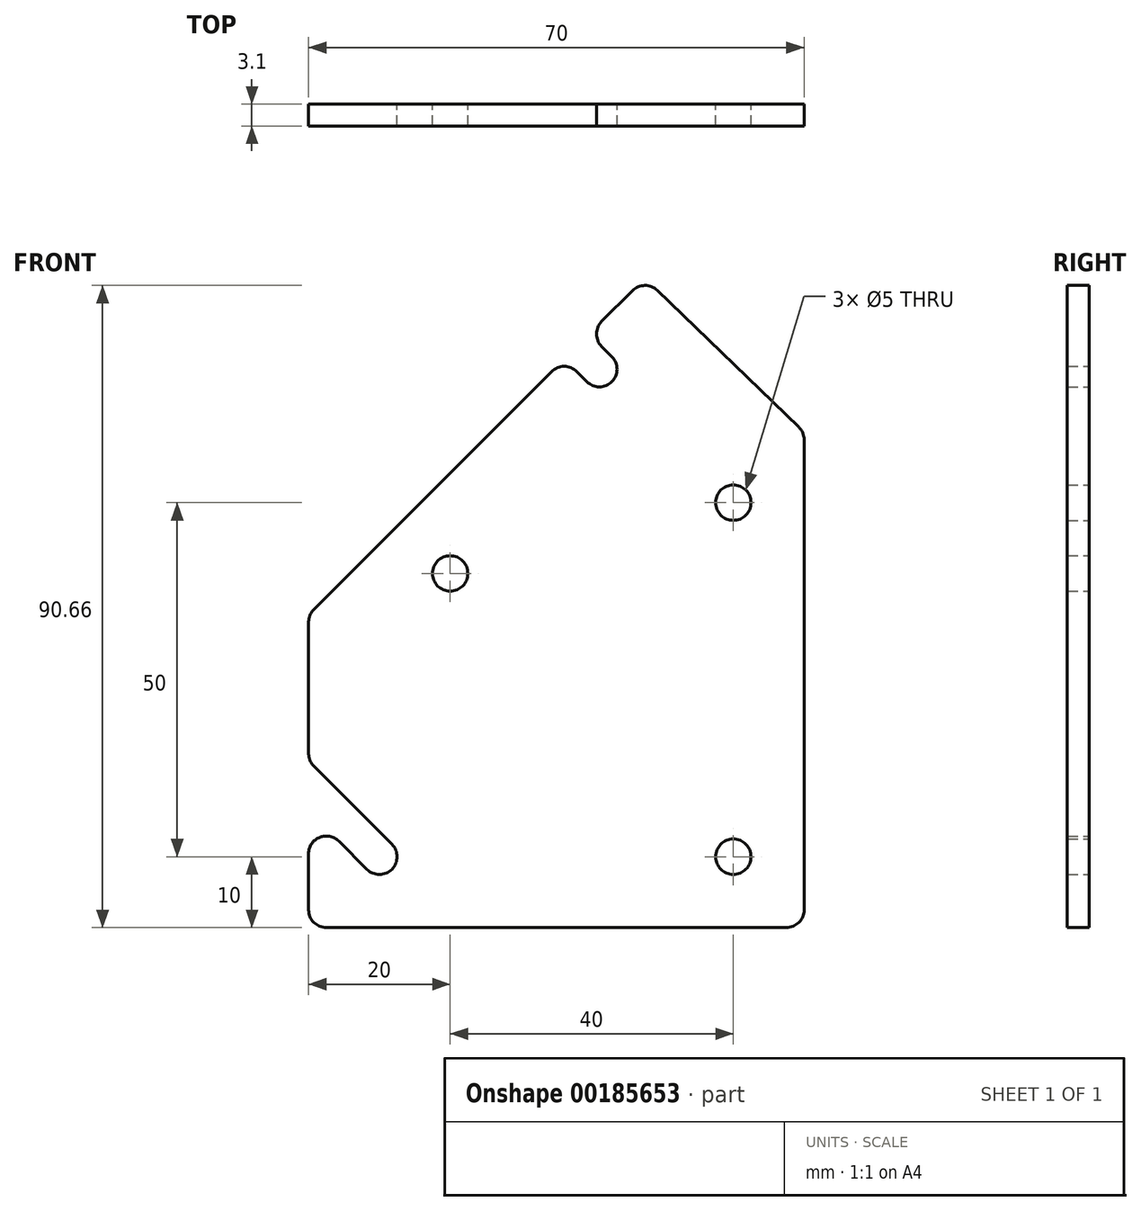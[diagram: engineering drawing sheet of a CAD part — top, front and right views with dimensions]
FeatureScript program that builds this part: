
annotation { "Feature Type Name" : "Feature", "Feature Type Description" : "" }
export const myFeature = defineFeature(function(context is Context, id is Id, definition is map)
    precondition{}
    {
        {
            var Q0;
            Q0=qCreatedBy(makeId("Front.planeOp"),FACE);
            var sketch = newSketch(context, id + "F0", { "sketchPlane" : qUnion([Q0])});
            skLineSegment(sketch, "E0", {"start": v(0, 0) * mm, "end": v(0, 69.94) * mm});
            skLineSegment(sketch, "E1", {"start": v(0, 69.94) * mm, "end": v(-22.5, 91.67) * mm});
            skLineSegment(sketch, "E2", {"start": v(-22.5, 91.67) * mm, "end": v(-30.36, 83.81) * mm});
            skLineSegment(sketch, "E3", {"start": v(-70, 44.17) * mm, "end": v(-70, 23.54) * mm});
            skLineSegment(sketch, "E4", {"start": v(-70, 0) * mm, "end": v(0, 0) * mm});
            skCircle(sketch, "E5", {"center": v(-10, 10) * mm, "radius": 2.5 * mm});
            skCircle(sketch, "E6", {"center": v(-10, 60) * mm, "radius": 2.5 * mm});
            skArc(sketch, "E7", {"start": v(-61.77, 8.23) * mm, "mid": v(-58.23, 8.23) * mm, "end": v(-58.23, 11.77) * mm});
            skCircle(sketch, "E8", {"center": v(-50, 50) * mm, "radius": 2.5 * mm});
            skArc(sketch, "E9", {"start": v(-30.69, 77.07) * mm, "mid": v(-27.15, 77.07) * mm, "end": v(-27.15, 80.6) * mm});
            skLineSegment(sketch, "E10", {"start": v(-27.15, 80.6) * mm, "end": v(-30.36, 83.81) * mm});
            skLineSegment(sketch, "E11", {"start": v(-30.69, 77.07) * mm, "end": v(-33.9, 80.28) * mm});
            skLineSegment(sketch, "E12.trimOffspring", {"start": v(-33.9, 80.28) * mm, "end": v(-70, 44.17) * mm});
            skLineSegment(sketch, "E13", {"start": v(-58.23, 11.77) * mm, "end": v(-70, 23.54) * mm});
            skLineSegment(sketch, "E14", {"start": v(-61.77, 8.23) * mm, "end": v(-70, 16.46) * mm});
            skLineSegment(sketch, "E15.trimOffspring", {"start": v(-70, 16.46) * mm, "end": v(-70, 0) * mm});
            skSolve(sketch);
        }
        {
            var Q0;
            Q0=makeQuery(id+"F0.imprint","IMPRINT",FACE,{"disambiguationData":[TD([[makeQuery(id+"F0.imprint","IMPRINT",EDGE,{"derivedFrom":sQuery(id+"F0.wireOp",EDGE,"E0")}),1.0]])]});
            extrude(context, id + "F1", {"entities" : qUnion([Q0]), "depth" : 3.1 * mm});
        }
        {
            var Q0;
            Q0=makeQuery(id+"F1.opExtrude","SWEPT_EDGE",EDGE,{"disambiguationData":[OSD([sQuery(id+"F0.wireOp",EDGE,"E2"),sQuery(id+"F0.wireOp",EDGE,"E10")])]});
            var Q1;
            Q1=makeQuery(id+"F1.opExtrude","SWEPT_EDGE",EDGE,{"disambiguationData":[OSD([sQuery(id+"F0.wireOp",EDGE,"E11"),sQuery(id+"F0.wireOp",EDGE,"E12.trimOffspring")])]});
            var Q2;
            Q2=makeQuery(id+"F1.opExtrude","SWEPT_EDGE",EDGE,{"disambiguationData":[OSD([sQuery(id+"F0.wireOp",EDGE,"E3"),sQuery(id+"F0.wireOp",EDGE,"E13")])]});
            var Q3;
            Q3=makeQuery(id+"F1.opExtrude","SWEPT_EDGE",EDGE,{"disambiguationData":[OSD([sQuery(id+"F0.wireOp",EDGE,"E14"),sQuery(id+"F0.wireOp",EDGE,"E15.trimOffspring")])]});
            var Q4;
            Q4=makeQuery(id+"F1.opExtrude","SWEPT_EDGE",EDGE,{"disambiguationData":[OSD([sQuery(id+"F0.wireOp",EDGE,"E4"),sQuery(id+"F0.wireOp",EDGE,"E15.trimOffspring")])]});
            var Q5;
            Q5=makeQuery(id+"F1.opExtrude","SWEPT_EDGE",EDGE,{"disambiguationData":[OSD([sQuery(id+"F0.wireOp",EDGE,"E1"),sQuery(id+"F0.wireOp",EDGE,"E2")])]});
            var Q6;
            Q6=makeQuery(id+"F1.opExtrude","SWEPT_EDGE",EDGE,{"disambiguationData":[OSD([sQuery(id+"F0.wireOp",EDGE,"E0"),sQuery(id+"F0.wireOp",EDGE,"E4")])]});
            var Q7;
            Q7=makeQuery(id+"F1.opExtrude","SWEPT_EDGE",EDGE,{"disambiguationData":[OSD([sQuery(id+"F0.wireOp",EDGE,"E0"),sQuery(id+"F0.wireOp",EDGE,"E1")])]});
            var Q8;
            Q8=makeQuery(id+"F1.opExtrude","SWEPT_EDGE",EDGE,{"disambiguationData":[OSD([sQuery(id+"F0.wireOp",EDGE,"E3"),sQuery(id+"F0.wireOp",EDGE,"E12.trimOffspring")])]});
            fillet(context, id + "F2", {"entities" : qUnion([Q0, Q1, Q2, Q3, Q4, Q5, Q6, Q7, Q8]), "radius" : 2.5 * mm, "tangentPropagation" : true, "allowEdgeOverflow" : false});
        }
    });
